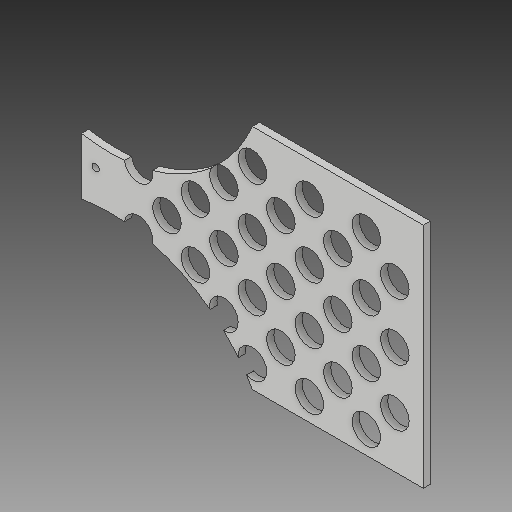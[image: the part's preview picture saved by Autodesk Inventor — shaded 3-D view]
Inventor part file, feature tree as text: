
AUTODESK INVENTOR PART (.ipt)
format: ipt  version: 2019 (Build 230136000, 136)  size: 259,072 bytes
history: native  units: in
note: dims shown in document units (in); Inventor stores cm internally (conversion verified against a paired STEP export)
features: sketch x4, extrude x2, hole x2, projected_geometry x1
ambient origin geometry x8: Origin, YZ Plane, XZ Plane, XY Plane, X Axis, Y Axis, Z Axis, Center Point
bodies: Solid1 (feature_tree)
feature tree (9):
  extrude  "Extrusion1"  Depth=4.0in
  hole  "Hole1"  [1 undecoded]
  hole  "Hole2"  [1 undecoded]
  extrude  "Extrusion2"  Depth=0.25in
  sketch  "Sketch1"  dims[d0=6.0in d1=4.0in]
  sketch  "Sketch2"  dims[d2=0.125in d3=0.0in d5=1.0in]
  sketch  "Sketch3"  dims[d6=1.9685in d8=1.0in d9=1.5748in d11=1.0in d14=1.9685in d16=1.0in d17=1.1811in d19=1.0in]
  sketch  "Sketch4"  dims[d22=0.5in d23=0.75in d24=0.375in d25=0.25in d26=0.5635in d27=1.0in d28=0.8108in d29=0.25in d30=0.125in d31=0.75in d32=0.375in d33=0.25in d34=0.5635in d35=1.0in d36=0.8108in d37=1.0in d38=0.0in d39=4.0in]
  projected_geometry  "Projected Loop1"
note: 2 required parameter values undecoded (feature->parameter linkage not recoverable at this tier; creation-order binding heuristic only, values carry confidence <= 0.55)
